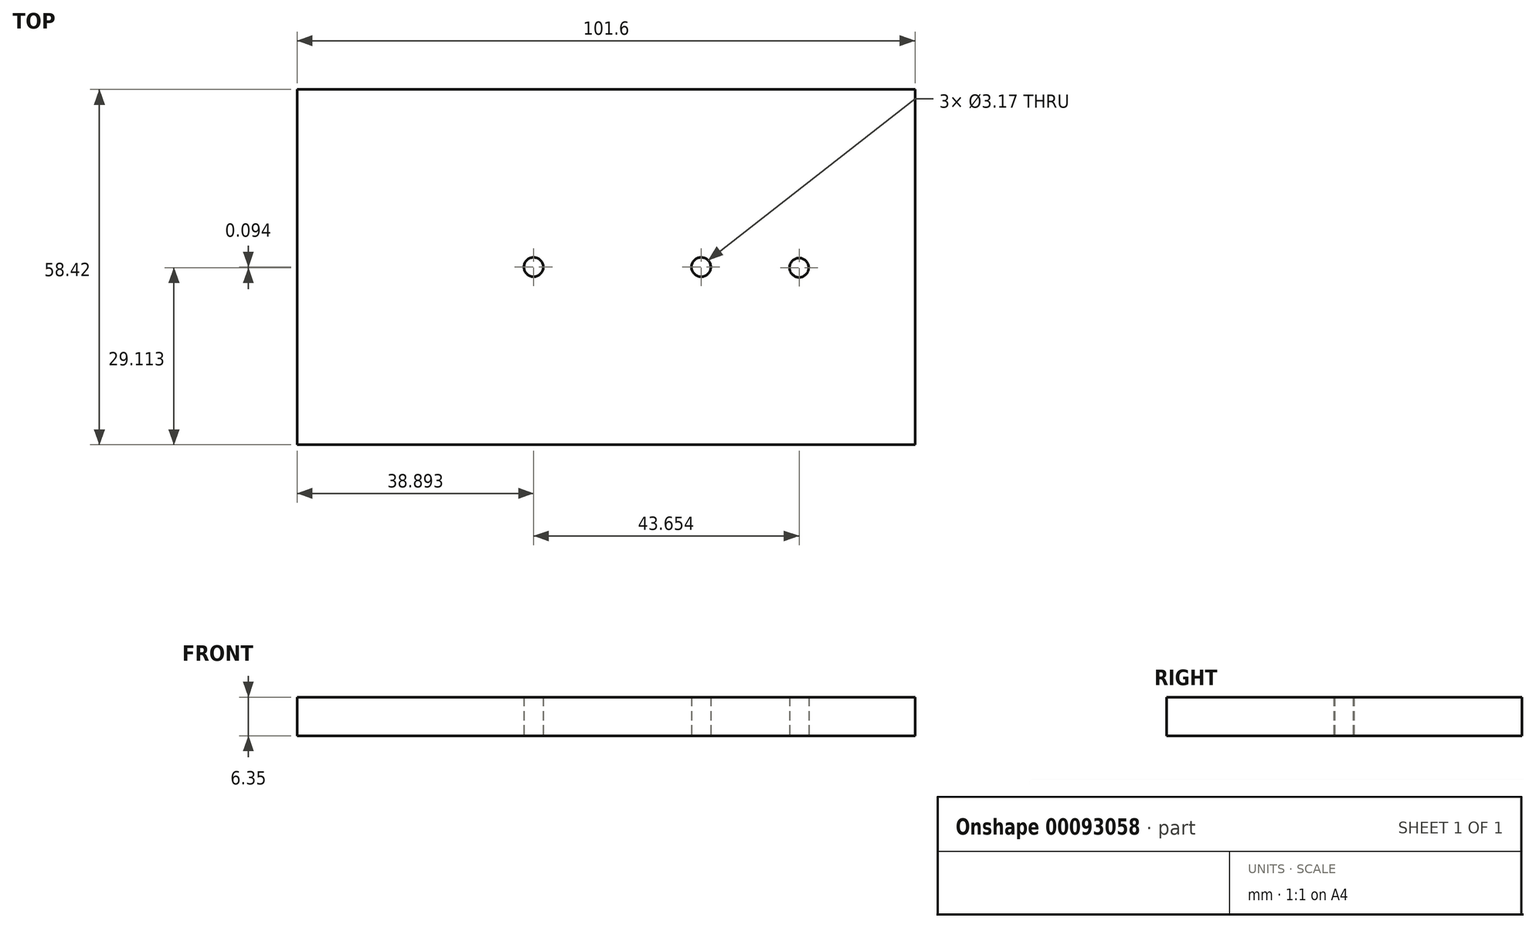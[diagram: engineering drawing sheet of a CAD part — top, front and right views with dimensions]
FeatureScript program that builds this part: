
annotation { "Feature Type Name" : "Feature", "Feature Type Description" : "" }
export const myFeature = defineFeature(function(context is Context, id is Id, definition is map)
    precondition{}
    {
        {
            var Q0;
            Q0=qCreatedBy(makeId("Top.planeOp"),FACE);
            var sketch = newSketch(context, id + "F0", { "sketchPlane" : qUnion([Q0])});
            skCircle(sketch, "E0", {"center": v(-16.35, -3.17) * mm, "radius": 19.05 * mm});
            skCircle(sketch, "E1", {"center": v(11.2, -3.17) * mm, "radius": 8.5 * mm});
            skLineSegment(sketch, "E2.bottom", {"start": v(-55.24, 26.04) * mm, "end": v(46.36, 26.04) * mm});
            skLineSegment(sketch, "E2.top", {"start": v(-55.24, -32.38) * mm, "end": v(46.36, -32.38) * mm});
            skLineSegment(sketch, "E2.left", {"start": v(-55.24, 26.04) * mm, "end": v(-55.24, -32.38) * mm});
            skLineSegment(sketch, "E2.right", {"start": v(46.36, 26.04) * mm, "end": v(46.36, -32.38) * mm});
            skCircle(sketch, "E3", {"center": v(27.3, -3.27) * mm, "radius": 7.15 * mm});
            skLineSegment(sketch, "E4", {"start": v(46.36, -3.17) * mm, "end": v(-55.24, -3.17) * mm});
            skLineSegment(sketch, "E5", {"start": v(-16.35, -3.17) * mm, "end": v(-16.35, 26.04) * mm});
            skLineSegment(sketch, "E6", {"start": v(11.2, -3.17) * mm, "end": v(11.2, 26.04) * mm});
            skLineSegment(sketch, "E7", {"start": v(27.3, -3.27) * mm, "end": v(27.3, 26.04) * mm});
            skCircle(sketch, "E8", {"center": v(-16.35, -3.17) * mm, "radius": 1.59 * mm});
            skCircle(sketch, "E9", {"center": v(11.2, -3.17) * mm, "radius": 1.59 * mm});
            skCircle(sketch, "E10", {"center": v(27.3, -3.27) * mm, "radius": 1.59 * mm});
            skSolve(sketch);
        }
        {
            var Q0;
            {var subQ0=sQuery(id+"F0.wireOp",EDGE,"E6");var subQ6=sQuery(id+"F0.wireOp",EDGE,"E1");var subQ11=makeQuery(id+"F0.imprint","INTERSECT",VERTEX,{"derivedFrom":[subQ6,subQ0]});Q0=makeQuery(id+"F0.imprint","IMPRINT",FACE,{"disambiguationData":[TD([[makeQuery(id+"F0.imprint","IMPRINT",EDGE,{"disambiguationData":[TD([[subQ11,1.0]])],"derivedFrom":subQ6}),-1.0]])]});}
            var Q1;
            {var subQ0=sQuery(id+"F0.wireOp",EDGE,"E7");var subQ1=sQuery(id+"F0.wireOp",EDGE,"E3");var subQ2=makeQuery(id+"F0.imprint","INTERSECT",VERTEX,{"derivedFrom":[subQ1,subQ0]});Q1=makeQuery(id+"F0.imprint","IMPRINT",FACE,{"disambiguationData":[TD([[makeQuery(id+"F0.imprint","IMPRINT",EDGE,{"disambiguationData":[TD([[subQ2,-1.0]])],"derivedFrom":subQ1}),1.0]])]});}
            var Q2;
            {var subQ0=sQuery(id+"F0.wireOp",EDGE,"E4");var subQ1=sQuery(id+"F0.wireOp",EDGE,"E1");var subQ2=makeQuery(id+"F0.imprint","INTERSECT",VERTEX,{"derivedFrom":[subQ1,subQ0]});Q2=makeQuery(id+"F0.imprint","IMPRINT",FACE,{"disambiguationData":[TD([[makeQuery(id+"F0.imprint","IMPRINT",EDGE,{"disambiguationData":[TD([[subQ2,-1.0]])],"derivedFrom":subQ0}),1.0]])]});}
            var Q3;
            {var subQ1=sQuery(id+"F0.wireOp",EDGE,"E2.top");Q3=makeQuery(id+"F0.imprint","IMPRINT",FACE,{"disambiguationData":[TD([[makeQuery(id+"F0.imprint","IMPRINT",EDGE,{"derivedFrom":subQ1}),1.0]])]});}
            var Q4;
            {var subQ0=sQuery(id+"F0.wireOp",EDGE,"E4");var subQ1=sQuery(id+"F0.wireOp",EDGE,"E3");var subQ2=makeQuery(id+"F0.imprint","INTERSECT",VERTEX,{"disambiguationData":[OD(0.0)],"derivedFrom":[subQ1,subQ0]});Q4=makeQuery(id+"F0.imprint","IMPRINT",FACE,{"disambiguationData":[TD([[makeQuery(id+"F0.imprint","IMPRINT",EDGE,{"disambiguationData":[TD([[subQ2,1.0]])],"derivedFrom":subQ1}),1.0]])]});}
            var Q5;
            {var subQ0=sQuery(id+"F0.wireOp",EDGE,"E6");var subQ1=sQuery(id+"F0.wireOp",EDGE,"E1");var subQ2=makeQuery(id+"F0.imprint","INTERSECT",VERTEX,{"derivedFrom":[subQ1,subQ0]});Q5=makeQuery(id+"F0.imprint","IMPRINT",FACE,{"disambiguationData":[TD([[makeQuery(id+"F0.imprint","IMPRINT",EDGE,{"disambiguationData":[TD([[subQ2,1.0]])],"derivedFrom":subQ1}),1.0]])]});}
            var Q6;
            {var subQ0=sQuery(id+"F0.wireOp",EDGE,"E7");var subQ1=sQuery(id+"F0.wireOp",EDGE,"E3");var subQ2=makeQuery(id+"F0.imprint","INTERSECT",VERTEX,{"derivedFrom":[subQ1,subQ0]});Q6=makeQuery(id+"F0.imprint","IMPRINT",FACE,{"disambiguationData":[TD([[makeQuery(id+"F0.imprint","IMPRINT",EDGE,{"disambiguationData":[TD([[subQ2,1.0]])],"derivedFrom":subQ1}),1.0]])]});}
            var Q7;
            {var subQ0=sQuery(id+"F0.wireOp",EDGE,"E5");var subQ1=sQuery(id+"F0.wireOp",EDGE,"E0");var subQ2=makeQuery(id+"F0.imprint","INTERSECT",VERTEX,{"derivedFrom":[subQ1,subQ0]});Q7=makeQuery(id+"F0.imprint","IMPRINT",FACE,{"disambiguationData":[TD([[makeQuery(id+"F0.imprint","IMPRINT",EDGE,{"disambiguationData":[TD([[subQ2,-1.0]])],"derivedFrom":subQ1}),1.0]])]});}
            var Q8;
            {var subQ0=sQuery(id+"F0.wireOp",EDGE,"E6");var subQ1=sQuery(id+"F0.wireOp",EDGE,"E1");var subQ2=makeQuery(id+"F0.imprint","INTERSECT",VERTEX,{"derivedFrom":[subQ1,subQ0]});Q8=makeQuery(id+"F0.imprint","IMPRINT",FACE,{"disambiguationData":[TD([[makeQuery(id+"F0.imprint","IMPRINT",EDGE,{"disambiguationData":[TD([[subQ2,1.0]])],"derivedFrom":subQ0}),1.0]])]});}
            var Q9;
            {var subQ0=sQuery(id+"F0.wireOp",EDGE,"E4");var subQ1=sQuery(id+"F0.wireOp",EDGE,"E0");var subQ2=makeQuery(id+"F0.imprint","INTERSECT",VERTEX,{"derivedFrom":[subQ1,subQ0]});Q9=makeQuery(id+"F0.imprint","IMPRINT",FACE,{"disambiguationData":[TD([[makeQuery(id+"F0.imprint","IMPRINT",EDGE,{"disambiguationData":[TD([[subQ2,1.0]])],"derivedFrom":subQ0}),1.0]])]});}
            var Q10;
            {var subQ5=sQuery(id+"F0.wireOp",EDGE,"E5");var subQ7=sQuery(id+"F0.wireOp",EDGE,"E0");var subQ9=makeQuery(id+"F0.imprint","INTERSECT",VERTEX,{"derivedFrom":[subQ7,subQ5]});Q10=makeQuery(id+"F0.imprint","IMPRINT",FACE,{"disambiguationData":[TD([[makeQuery(id+"F0.imprint","IMPRINT",EDGE,{"disambiguationData":[TD([[subQ9,-1.0]])],"derivedFrom":subQ7}),-1.0]])]});}
            var Q11;
            {var subQ1=sQuery(id+"F0.wireOp",EDGE,"E2.right");var subQ7=sQuery(id+"F0.wireOp",EDGE,"E2.bottom");var subQ8=makeQuery(id+"F0.imprint","INTERSECT",VERTEX,{"derivedFrom":[subQ7,subQ1]});Q11=makeQuery(id+"F0.imprint","IMPRINT",FACE,{"disambiguationData":[TD([[makeQuery(id+"F0.imprint","IMPRINT",EDGE,{"disambiguationData":[TD([[subQ8,1.0]])],"derivedFrom":subQ7}),-1.0]])]});}
            var Q12;
            {var subQ0=sQuery(id+"F0.wireOp",EDGE,"E5");var subQ1=sQuery(id+"F0.wireOp",EDGE,"E2.bottom");var subQ2=makeQuery(id+"F0.imprint","INTERSECT",VERTEX,{"derivedFrom":[subQ1,subQ0]});Q12=makeQuery(id+"F0.imprint","IMPRINT",FACE,{"disambiguationData":[TD([[makeQuery(id+"F0.imprint","IMPRINT",EDGE,{"disambiguationData":[TD([[subQ2,-1.0]])],"derivedFrom":subQ1}),-1.0]])]});}
            var Q13;
            {var subQ0=sQuery(id+"F0.wireOp",EDGE,"E5");var subQ1=sQuery(id+"F0.wireOp",EDGE,"E0");var subQ2=makeQuery(id+"F0.imprint","INTERSECT",VERTEX,{"derivedFrom":[subQ1,subQ0]});Q13=makeQuery(id+"F0.imprint","IMPRINT",FACE,{"disambiguationData":[TD([[makeQuery(id+"F0.imprint","IMPRINT",EDGE,{"disambiguationData":[TD([[subQ2,1.0]])],"derivedFrom":subQ0}),-1.0]])]});}
            var Q14;
            Q14=sQuery(id+"F0.wireOp",EDGE,"E0");
            var Q15;
            Q15=sQuery(id+"F0.wireOp",EDGE,"E1");
            var Q16;
            Q16=sQuery(id+"F0.wireOp",EDGE,"E2.bottom");
            var Q17;
            Q17=sQuery(id+"F0.wireOp",EDGE,"E2.top");
            var Q18;
            Q18=sQuery(id+"F0.wireOp",EDGE,"E2.left");
            var Q19;
            Q19=sQuery(id+"F0.wireOp",EDGE,"E2.right");
            var Q20;
            Q20=sQuery(id+"F0.wireOp",EDGE,"E3");
            var Q21;
            Q21=sQuery(id+"F0.wireOp",EDGE,"E4");
            var Q22;
            Q22=sQuery(id+"F0.wireOp",EDGE,"E5");
            var Q23;
            Q23=sQuery(id+"F0.wireOp",EDGE,"E6");
            var Q24;
            Q24=sQuery(id+"F0.wireOp",EDGE,"E7");
            extrude(context, id + "F1", {"entities" : qUnion([Q0, Q1, Q2, Q3, Q4, Q5, Q6, Q7, Q8, Q9, Q10, Q11, Q12, Q13]), "surfaceEntities" : qUnion([Q14, Q15, Q16, Q17, Q18, Q19, Q20, Q21, Q22, Q23, Q24]), "depth" : 6.35 * mm});
        }
    });
